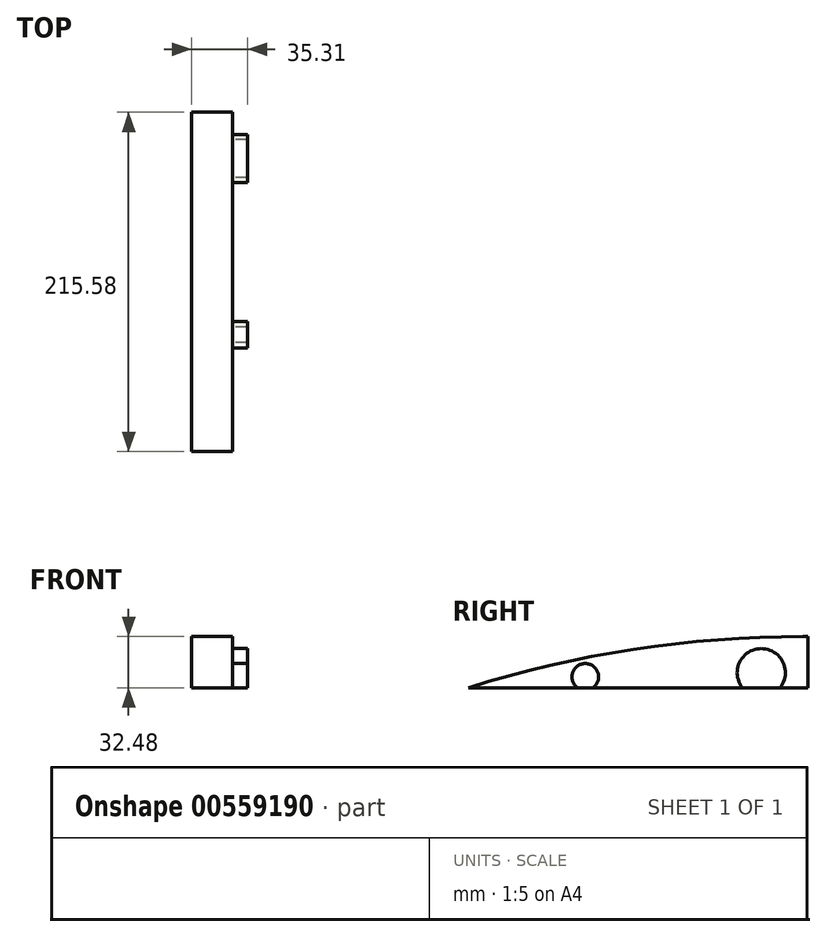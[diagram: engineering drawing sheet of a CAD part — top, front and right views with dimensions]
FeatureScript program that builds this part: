
annotation { "Feature Type Name" : "Feature", "Feature Type Description" : "" }
export const myFeature = defineFeature(function(context is Context, id is Id, definition is map)
    precondition{}
    {
        {
            var Q0;
            Q0=qCreatedBy(makeId("Right.planeOp"),FACE);
            var sketch = newSketch(context, id + "F0", { "sketchPlane" : qUnion([Q0])});
            skLineSegment(sketch, "E0.bottom", {"start": v(94.37, 32.48) * mm, "end": v(-121.21, 32.48) * mm});
            skLineSegment(sketch, "E0.top", {"start": v(94.37, 0) * mm, "end": v(-121.21, 0) * mm});
            skLineSegment(sketch, "E0.left", {"start": v(94.37, 32.48) * mm, "end": v(94.37, 0) * mm});
            skLineSegment(sketch, "E0.right", {"start": v(-121.21, 32.48) * mm, "end": v(-121.21, 0) * mm});
            skSolve(sketch);
        }
        {
            var Q0;
            Q0=makeQuery(id+"F0.imprint","IMPRINT",FACE,{"disambiguationData":[TD([[makeQuery(id+"F0.imprint","IMPRINT",EDGE,{"derivedFrom":sQuery(id+"F0.wireOp",EDGE,"E0.bottom")}),1.0]])]});
            extrude(context, id + "F1", {"entities" : qUnion([Q0]), "oppositeDirection" : true, "depth" : 25.9 * mm, "offsetDistance" : 25.4 * mm});
        }
        {
            var Q0;
            Q0=makeQuery(id+"F1.opExtrude","SWEPT_EDGE",EDGE,{"disambiguationData":[OSD([sQuery(id+"F0.wireOp",EDGE,"E0.bottom"),sQuery(id+"F0.wireOp",EDGE,"E0.right")])]});
            fillet(context, id + "F2", {"entities" : qUnion([Q0]), "radius" : 710.7 * mm, "tangentPropagation" : true, "allowEdgeOverflow" : false});
        }
        {
            var Q0;
            Q0=makeQuery(id+"F1.opExtrude","CAP_FACE",FACE,{"disambiguationData":[OSD([sQuery(id+"F0.wireOp",EDGE,"E0.bottom"),sQuery(id+"F0.wireOp",EDGE,"E0.top"),sQuery(id+"F0.wireOp",EDGE,"E0.left"),sQuery(id+"F0.wireOp",EDGE,"E0.right")])],"isStart":true});
            var sketch = newSketch(context, id + "F3", { "sketchPlane" : qUnion([Q0])});
            skCircle(sketch, "E1", {"center": v(-46.9, 6.87) * mm, "radius": 8.47 * mm});
            skCircle(sketch, "E2", {"center": v(64.9, 9.54) * mm, "radius": 15.3 * mm});
            skSolve(sketch);
        }
        {
            var Q0;
            {var subQ0=sQuery(id+"F3.wireOp",EDGE,"E1");var subQ1=makeQuery(id+"F1.opExtrude","CAP_EDGE",EDGE,{"disambiguationData":[OSD([sQuery(id+"F0.wireOp",EDGE,"E0.top")])],"isStart":true});var subQ2=makeQuery(id+"F3.imprint","INTERSECT",VERTEX,{"disambiguationData":[OD(0.0)],"derivedFrom":[subQ1,subQ0]});Q0=makeQuery(id+"F3.imprint","IMPRINT",FACE,{"disambiguationData":[TD([[makeQuery(id+"F3.imprint","IMPRINT",EDGE,{"disambiguationData":[TD([[subQ2,1.0]])],"derivedFrom":subQ0}),1.0]])]});}
            var Q1;
            {var subQ0=sQuery(id+"F3.wireOp",EDGE,"E2");var subQ1=makeQuery(id+"F1.opExtrude","CAP_EDGE",EDGE,{"disambiguationData":[OSD([sQuery(id+"F0.wireOp",EDGE,"E0.top")])],"isStart":true});var subQ2=makeQuery(id+"F3.imprint","INTERSECT",VERTEX,{"disambiguationData":[OD(0.0)],"derivedFrom":[subQ1,subQ0]});Q1=makeQuery(id+"F3.imprint","IMPRINT",FACE,{"disambiguationData":[TD([[makeQuery(id+"F3.imprint","IMPRINT",EDGE,{"disambiguationData":[TD([[subQ2,-1.0]])],"derivedFrom":subQ0}),1.0]])]});}
            extrude(context, id + "F4", {"entities" : qUnion([Q0, Q1]), "operationType" : NewBodyOperationType.ADD, "depth" : 9.4 * mm, "offsetDistance" : 25.4 * mm});
        }
    });
